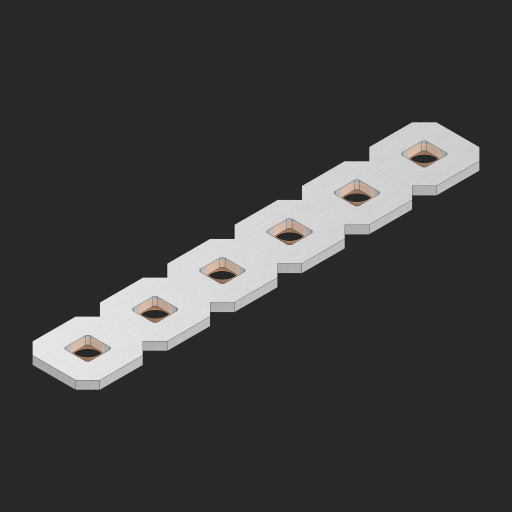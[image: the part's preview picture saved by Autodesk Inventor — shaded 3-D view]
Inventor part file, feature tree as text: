
AUTODESK INVENTOR PART (.ipt)
format: ipt  version: 2023 (Build 270158000, 158)  size: 332,800 bytes
history: native  units: in
note: dims shown in document units (in); Inventor stores cm internally (conversion verified against a paired STEP export)
features: other x7, extrude x5, sketch x2, pattern_linear x1
ambient origin geometry x8: Origin, YZ Plane, XZ Plane, XY Plane, X Axis, Y Axis, Z Axis, Center Point
bodies: Solid1 (feature_tree), Body (feature_tree)
feature tree (15):
  pattern_linear  "Rectangular Pattern1"  Spacing1=0.09in  [1 undecoded]
  sketch  "Sketch1"  dims[d1=0.5in]
  sketch  "Sketch2"  dims[d2=0.182in d3=0.09in d4=0.09in d5=0.09in d6=0.09in d7=0.09in d8=0.09in d9=0.09in d10=0.09in d11=0.02in d13=0.0in d14=0.172in d15=0.0625in d16=0.0in d19=0.5in d22=0.5in]
  other  "Srf1"
  other  "Srf126"
  other  "Srf127"
  other  "Srf128"
  other  "Srf129"
  other  "Srf130"
  other  "Circle"
  extrude  "ExtrusionSrf126"  Depth=0.09in
  extrude  "ExtrusionSrf127"  Depth=0.09in
  extrude  "ExtrusionSrf128"  Depth=0.09in
  extrude  "ExtrusionSrf129"  Depth=0.09in
  extrude  "ExtrusionSrf130"  Depth=0.09in
note: 1 required parameter value undecoded (feature->parameter linkage not recoverable at this tier; creation-order binding heuristic only, values carry confidence <= 0.55)
